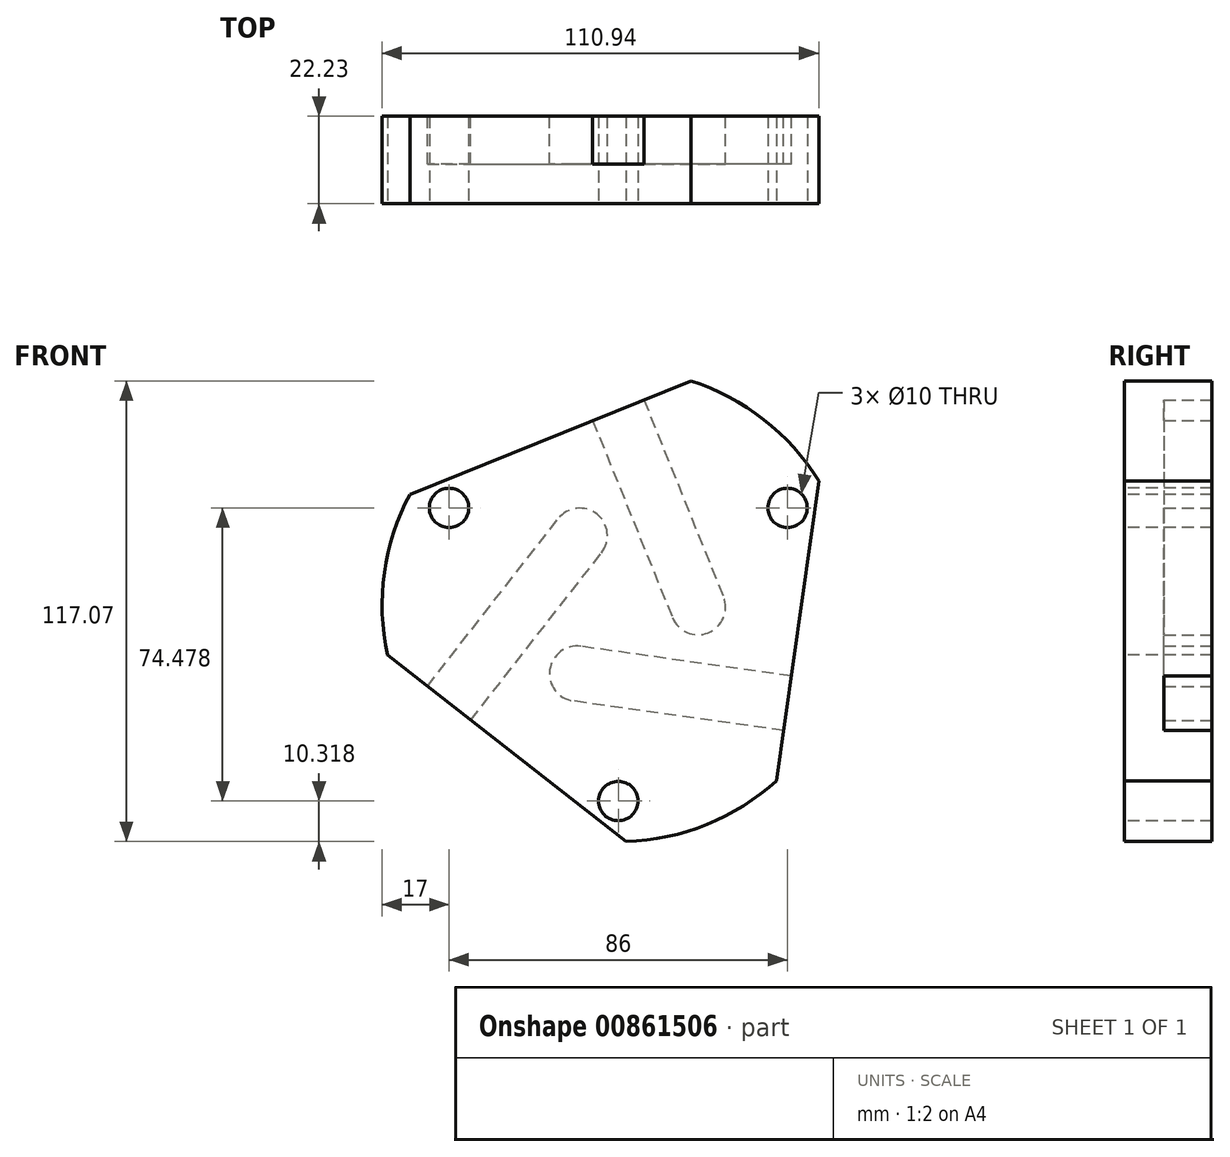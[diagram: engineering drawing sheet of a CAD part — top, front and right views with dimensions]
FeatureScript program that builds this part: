
annotation { "Feature Type Name" : "Feature", "Feature Type Description" : "" }
export const myFeature = defineFeature(function(context is Context, id is Id, definition is map)
    precondition{}
    {
        {
            var Q0;
            Q0=qCreatedBy(makeId("Front.planeOp"),FACE);
            var sketch = newSketch(context, id + "F0", { "sketchPlane" : qUnion([Q0])});
            skCircle(sketch, "E0", {"center": v(-43, 24.83) * mm, "radius": 5 * mm});
            skCircle(sketch, "E1", {"center": v(43, 24.83) * mm, "radius": 5 * mm});
            skCircle(sketch, "E2", {"center": v(0, -49.65) * mm, "radius": 5 * mm});
            skArc(sketch, "E3", {"start": v(-52.92, 28.27) * mm, "mid": v(-59.42, 8.35) * mm, "end": v(-58.66, -12.59) * mm});
            skArc(sketch, "E4.trimOffspring", {"start": v(50.94, 31.7) * mm, "mid": v(36.94, 47.28) * mm, "end": v(18.43, 57.1) * mm});
            skArc(sketch, "E5.trimOffspring", {"start": v(1.98, -59.97) * mm, "mid": v(22.48, -55.63) * mm, "end": v(40.23, -44.51) * mm});
            skLineSegment(sketch, "E6", {"start": v(50.94, 31.7) * mm, "end": v(40.23, -44.51) * mm});
            skLineSegment(sketch, "E7.1.0", {"start": v(-52.92, 28.27) * mm, "end": v(18.43, 57.1) * mm});
            skLineSegment(sketch, "E7.2.0", {"start": v(1.98, -59.97) * mm, "end": v(-58.66, -12.59) * mm});
            skSolve(sketch);
        }
        {
            var Q0;
            Q0 = qSketchRegion(id + "F0", true);
            extrude(context, id + "F1", {"entities" : qUnion([Q0]), "oppositeDirection" : true, "depth" : (.875 * 25.4) * mm, "offsetDistance" : 25 * mm});
        }
        {
            var Q0;
            Q0=makeQuery(id+"F1.opExtrude","CAP_FACE",FACE,{"disambiguationData":[OSD([sQuery(id+"F0.wireOp",EDGE,"E0"),sQuery(id+"F0.wireOp",EDGE,"E1"),sQuery(id+"F0.wireOp",EDGE,"E2"),sQuery(id+"F0.wireOp",EDGE,"E3"),sQuery(id+"F0.wireOp",EDGE,"yU9tSEUy-AP5L-bvQa-001X-A80d9pAAhO38"),sQuery(id+"F0.wireOp",EDGE,"0402db88-7d6a-4b16-b3f2-a8e9761683bf.1.0"),sQuery(id+"F0.wireOp",EDGE,"0402db88-7d6a-4b16-b3f2-a8e9761683bf.2.0"),sQuery(id+"F0.wireOp",EDGE,"E4.trimOffspring"),sQuery(id+"F0.wireOp",EDGE,"E5.trimOffspring")])],"isStart":false});
            var sketch = newSketch(context, id + "F2", { "sketchPlane" : qUnion([Q0])});
            skPoint(sketch, "E8.center", {"position": v(0, 0) * mm});
            skArc(sketch, "E9", {"start": v(11.45, -24.24) * mm, "mid": v(17.4, -16.34) * mm, "end": v(9.5, -10.38) * mm});
            skLineSegment(sketch, "E10", {"start": v(-43.97, -17.9) * mm, "end": v(9.5, -10.38) * mm});
            skLineSegment(sketch, "E11", {"start": v(-42.03, -31.76) * mm, "end": v(11.45, -24.24) * mm});
            skLineSegment(sketch, "E12", {"start": v(-43.97, -17.9) * mm, "end": v(-42.03, -31.76) * mm});
            skPoint(sketch, "E13.center.orphan", {"position": v(-43, 24.83) * mm});
            skLineSegment(sketch, "E14.1.0", {"start": v(37.48, -29.14) * mm, "end": v(48.52, -20.52) * mm});
            skLineSegment(sketch, "E14.1.1", {"start": v(37.48, -29.14) * mm, "end": v(4.24, 13.42) * mm});
            skArc(sketch, "E14.1.2", {"start": v(15.27, 22.04) * mm, "mid": v(5.44, 23.24) * mm, "end": v(4.24, 13.42) * mm});
            skLineSegment(sketch, "E14.1.3", {"start": v(48.52, -20.52) * mm, "end": v(15.27, 22.04) * mm});
            skLineSegment(sketch, "E14.2.0", {"start": v(6.5, 47.03) * mm, "end": v(-6.5, 52.27) * mm});
            skLineSegment(sketch, "E14.2.1", {"start": v(6.5, 47.03) * mm, "end": v(-13.74, -3.04) * mm});
            skArc(sketch, "E14.2.2", {"start": v(-26.72, 2.2) * mm, "mid": v(-22.85, -6.9) * mm, "end": v(-13.74, -3.04) * mm});
            skLineSegment(sketch, "E14.2.3", {"start": v(-6.5, 52.27) * mm, "end": v(-26.72, 2.2) * mm});
            skSolve(sketch);
        }
        {
            var Q0;
            Q0 = qSketchRegion(id + "F2", true);
            extrude(context, id + "F3", {"entities" : qUnion([Q0]), "operationType" : NewBodyOperationType.REMOVE, "oppositeDirection" : true, "depth" : 12.2 * mm, "offsetDistance" : 25 * mm});
        }
    });
